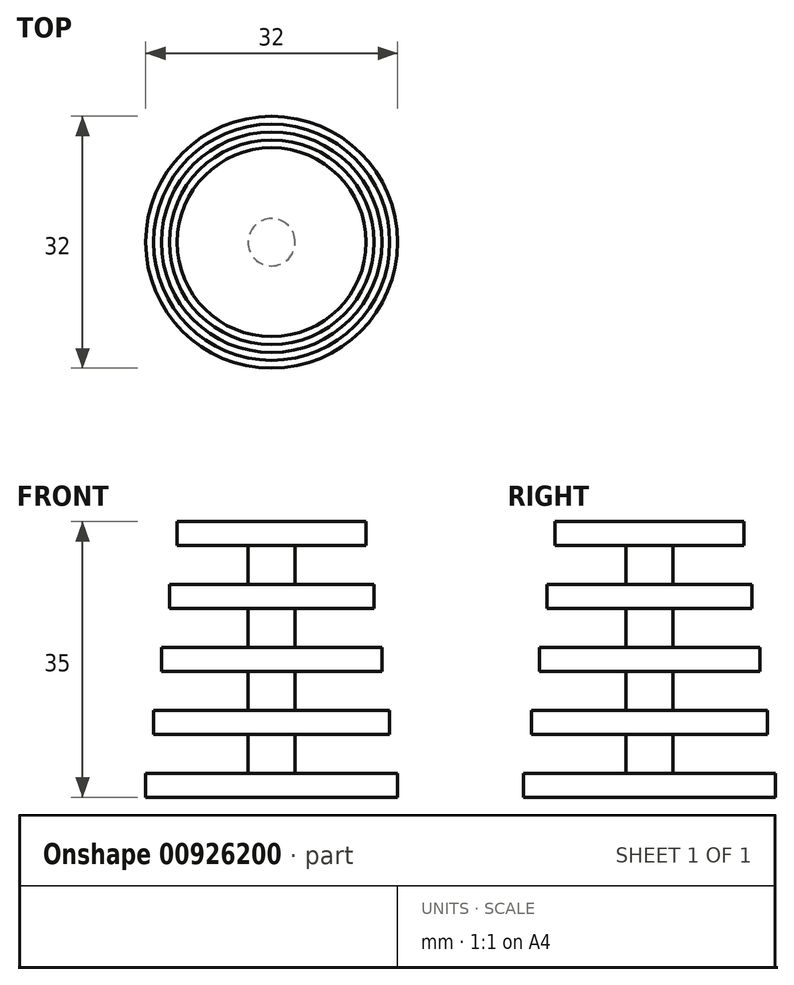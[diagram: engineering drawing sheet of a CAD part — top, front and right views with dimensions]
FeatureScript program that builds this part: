
annotation { "Feature Type Name" : "Feature", "Feature Type Description" : "" }
export const myFeature = defineFeature(function(context is Context, id is Id, definition is map)
    precondition{}
    {
        {
            var Q0;
            Q0=qCreatedBy(makeId("Right.planeOp"),FACE);
            var sketch = newSketch(context, id + "F0", { "sketchPlane" : qUnion([Q0])});
            skLineSegment(sketch, "E0", {"start": v(16, 0) * mm, "end": v(16, 3) * mm});
            skLineSegment(sketch, "E1", {"start": v(16, 3) * mm, "end": v(3, 3) * mm});
            skLineSegment(sketch, "E2", {"start": v(3, 3) * mm, "end": v(3, 8) * mm});
            skLineSegment(sketch, "E3", {"start": v(3, 8) * mm, "end": v(15, 8) * mm});
            skLineSegment(sketch, "E4", {"start": v(15, 8) * mm, "end": v(15, 11) * mm});
            skLineSegment(sketch, "E5", {"start": v(15, 11) * mm, "end": v(3, 11) * mm});
            skLineSegment(sketch, "E6", {"start": v(3, 11) * mm, "end": v(3, 16) * mm});
            skLineSegment(sketch, "E7", {"start": v(3, 16) * mm, "end": v(14, 16) * mm});
            skLineSegment(sketch, "E8", {"start": v(14, 16) * mm, "end": v(14, 19) * mm});
            skLineSegment(sketch, "E9", {"start": v(14, 19) * mm, "end": v(3, 19) * mm});
            skLineSegment(sketch, "E10", {"start": v(3, 19) * mm, "end": v(3, 24) * mm});
            skLineSegment(sketch, "E11", {"start": v(3, 24) * mm, "end": v(13, 24) * mm});
            skLineSegment(sketch, "E12", {"start": v(13, 24) * mm, "end": v(13, 27) * mm});
            skLineSegment(sketch, "E13", {"start": v(13, 27) * mm, "end": v(3, 27) * mm});
            skLineSegment(sketch, "E14", {"start": v(3, 27) * mm, "end": v(3, 32) * mm});
            skLineSegment(sketch, "E15", {"start": v(3, 32) * mm, "end": v(12, 32) * mm});
            skLineSegment(sketch, "E16", {"start": v(12, 32) * mm, "end": v(12, 35) * mm});
            skLineSegment(sketch, "E17", {"start": v(12, 35) * mm, "end": v(0, 35) * mm});
            skLineSegment(sketch, "E18", {"start": v(0, 35) * mm, "end": v(0, 0) * mm});
            skLineSegment(sketch, "E19", {"start": v(16, 0) * mm, "end": v(0, 0) * mm});
            skSolve(sketch);
        }
        {
            var Q0;
            Q0=makeQuery(id+"F0.imprint","IMPRINT",FACE,{"disambiguationData":[TD([[makeQuery(id+"F0.imprint","IMPRINT",EDGE,{"derivedFrom":sQuery(id+"F0.wireOp",EDGE,"E0")}),1.0]])]});
            var Q1;
            Q1=sQuery(id+"F0.wireOp",EDGE,"E18");
            revolve(context, id + "F1", {"surfaceOperationType" : NewSurfaceOperationType.NEW, "entities" : qUnion([Q0]), "axis" : qUnion([Q1]), "revolveType" : RevolveType.FULL});
        }
    });
